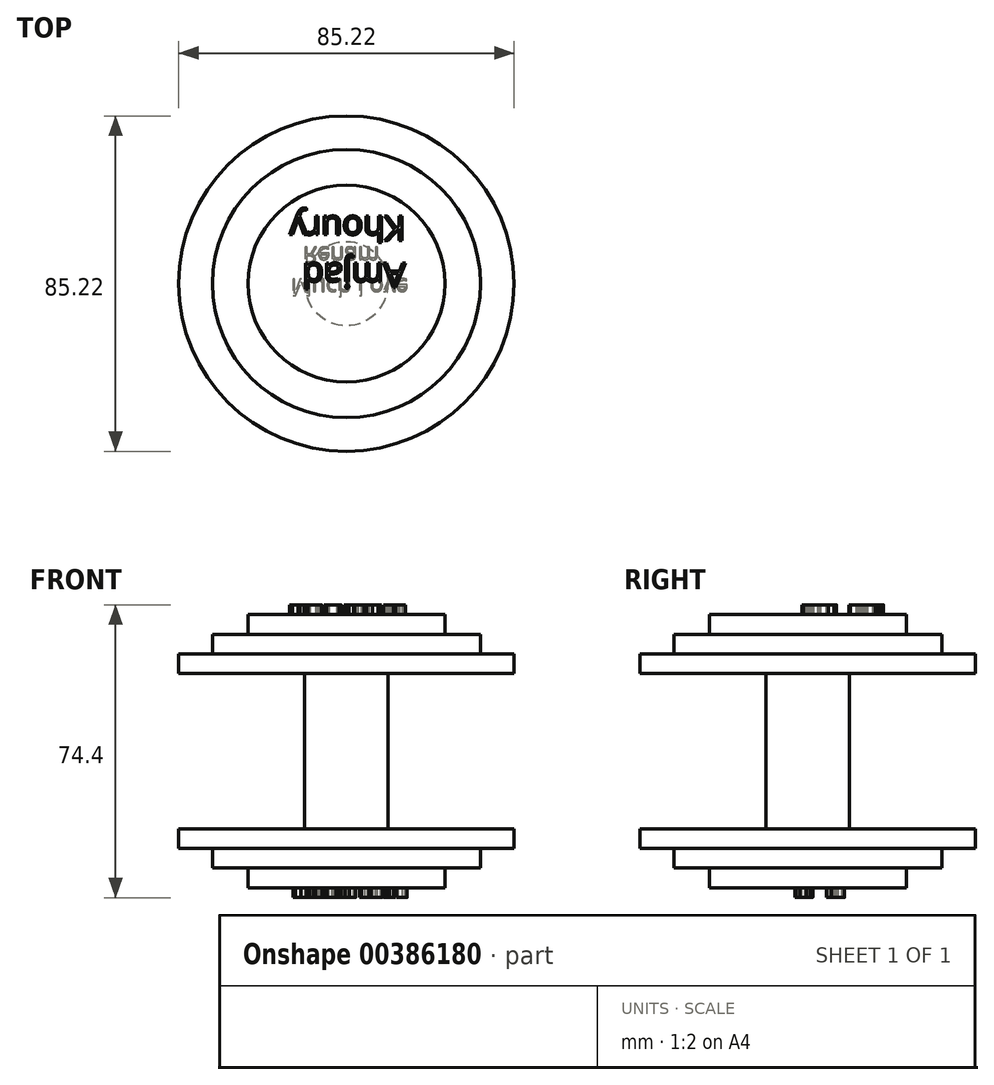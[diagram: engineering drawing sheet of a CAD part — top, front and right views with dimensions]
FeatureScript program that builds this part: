
annotation { "Feature Type Name" : "Feature", "Feature Type Description" : "" }
export const myFeature = defineFeature(function(context is Context, id is Id, definition is map)
    precondition{}
    {
        {
            var Q0;
            Q0=qCreatedBy(makeId("Right.planeOp"),FACE);
            var sketch = newSketch(context, id + "F0", { "sketchPlane" : qUnion([Q0])});
            skLineSegment(sketch, "E0", {"start": v(0, 45.9) * mm, "end": v(25, 45.9) * mm});
            skLineSegment(sketch, "E1", {"start": v(25, 45.9) * mm, "end": v(25, 40.9) * mm});
            skLineSegment(sketch, "E2", {"start": v(25, 40.9) * mm, "end": v(34.06, 40.9) * mm});
            skLineSegment(sketch, "E3", {"start": v(34.06, 40.9) * mm, "end": v(34.06, 35.9) * mm});
            skLineSegment(sketch, "E4", {"start": v(34.06, 35.9) * mm, "end": v(42.6, 35.9) * mm});
            skLineSegment(sketch, "E5", {"start": v(42.6, 35.9) * mm, "end": v(42.6, 30.9) * mm});
            skLineSegment(sketch, "E6", {"start": v(42.6, 30.9) * mm, "end": v(10.6, 30.9) * mm});
            skLineSegment(sketch, "E7", {"start": v(10.6, 30.9) * mm, "end": v(10.6, -8.5) * mm});
            skLineSegment(sketch, "E8", {"start": v(10.6, -8.5) * mm, "end": v(42.6, -8.5) * mm});
            skLineSegment(sketch, "E9", {"start": v(42.6, -8.5) * mm, "end": v(42.6, -13.5) * mm});
            skLineSegment(sketch, "E10", {"start": v(42.6, -13.5) * mm, "end": v(34.06, -13.5) * mm});
            skLineSegment(sketch, "E11", {"start": v(34.06, -13.5) * mm, "end": v(34.06, -18.5) * mm});
            skLineSegment(sketch, "E12", {"start": v(34.06, -18.5) * mm, "end": v(25, -18.5) * mm});
            skLineSegment(sketch, "E13", {"start": v(25, -18.5) * mm, "end": v(25, -23.5) * mm});
            skLineSegment(sketch, "E14", {"start": v(25, -23.5) * mm, "end": v(0, -23.5) * mm});
            skLineSegment(sketch, "E15", {"start": v(25, 45.9) * mm, "end": v(17.6, 45.9) * mm});
            skLineSegment(sketch, "E16", {"start": v(0, 45.9) * mm, "end": v(0, -23.5) * mm});
            skSolve(sketch);
        }
        {
            var Q0;
            Q0 = qSketchRegion(id + "F0", true);
            var Q1;
            Q1=sQuery(id+"F0.wireOp",EDGE,"E16");
            revolve(context, id + "F1", {"entities" : qUnion([Q0]), "axis" : qUnion([Q1]), "revolveType" : RevolveType.FULL});
        }
        {
            var Q0;
            Q0=makeQuery(id+"F1.opRevolve","SWEPT_FACE",FACE,{"disambiguationData":[OSD([sQuery(id+"F0.wireOp",EDGE,"E14")])]});
            var sketch = newSketch(context, id + "F2", { "sketchPlane" : qUnion([Q0])});
            skText(sketch, "E17", { "text": "Much Love\n  Reham", "fontName": "OpenSans-Regular.ttf"});
            const initialGuessF2  = {"E17": [-0.0142, -0.0012, 1, 0, 0.00427]};
            skSetInitialGuess(sketch, initialGuessF2);
            skSolve(sketch);
        }
        {
            var Q0;
            Q0 = qSketchRegion(id + "F2", true);
            extrude(context, id + "F3", {"entities" : qUnion([Q0]), "operationType" : NewBodyOperationType.ADD, "depth" : 2.5 * mm});
        }
        {
            var Q0;
            Q0=makeQuery(id+"F1.opRevolve","SWEPT_FACE",FACE,{"disambiguationData":[OSD([sQuery(id+"F0.wireOp",EDGE,"E0"),sQuery(id+"F0.wireOp",EDGE,"E15")])]});
            var sketch = newSketch(context, id + "F4", { "sketchPlane" : qUnion([Q0])});
            skSolve(sketch);
        }
        {
            var Q0;
            Q0=makeQuery(id+"F4.imprint","IMPRINT",FACE,{"disambiguationData":[TD([[makeQuery(id+"F4.imprint","IMPRINT",EDGE,{"derivedFrom":makeQuery(id+"F1.opRevolve","SWEPT_EDGE",EDGE,{"disambiguationData":[OSD([sQuery(id+"F0.wireOp",EDGE,"E1"),sQuery(id+"F0.wireOp",EDGE,"E15")])]})}),1.0]])]});
            var sketch = newSketch(context, id + "F5", { "sketchPlane" : qUnion([Q0])});
            skText(sketch, "E18", { "text": "Amjad\nKhoury", "fontName": "OpenSans-Regular.ttf"});
            const initialGuessF5  = {"E18": [0.015, 0.00522, -1, 0, 0.00631]};
            skSetInitialGuess(sketch, initialGuessF5);
            skSolve(sketch);
        }
        {
            var Q0;
            Q0 = qSketchRegion(id + "F5", true);
            extrude(context, id + "F6", {"entities" : qUnion([Q0]), "operationType" : NewBodyOperationType.ADD, "depth" : 2.5 * mm});
        }
    });
